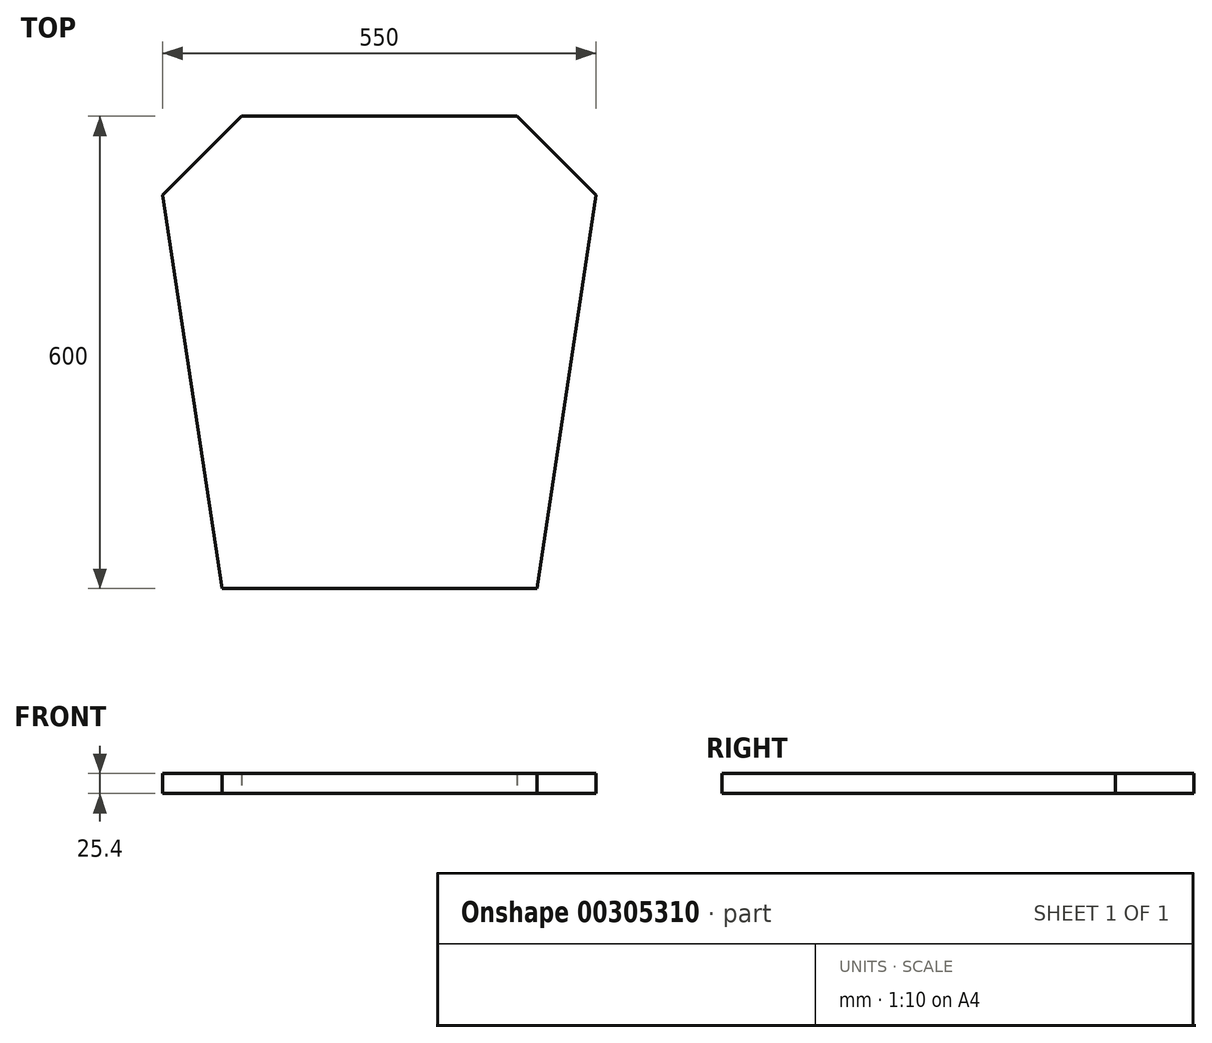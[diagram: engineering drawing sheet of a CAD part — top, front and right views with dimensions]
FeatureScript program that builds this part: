
annotation { "Feature Type Name" : "Feature", "Feature Type Description" : "" }
export const myFeature = defineFeature(function(context is Context, id is Id, definition is map)
    precondition{}
    {
        {
            var Q0;
            Q0=qCreatedBy(makeId("Top.planeOp"),FACE);
            var sketch = newSketch(context, id + "F0", { "sketchPlane" : qUnion([Q0])});
            skLineSegment(sketch, "E0", {"start": v(-175, 182.37) * mm, "end": v(175, 182.37) * mm});
            skLineSegment(sketch, "E1", {"start": v(175, 182.37) * mm, "end": v(275, 82.37) * mm});
            skLineSegment(sketch, "E2", {"start": v(275, 82.37) * mm, "end": v(200, -417.63) * mm});
            skLineSegment(sketch, "E3", {"start": v(200, -417.63) * mm, "end": v(-200, -417.63) * mm});
            skLineSegment(sketch, "E4", {"start": v(-200, -417.63) * mm, "end": v(-275, 82.37) * mm});
            skLineSegment(sketch, "E5", {"start": v(-275, 82.37) * mm, "end": v(-175, 182.37) * mm});
            skLineSegment(sketch, "E6", {"start": v(0, 182.37) * mm, "end": v(0, -417.63) * mm});
            skLineSegment(sketch, "E7", {"start": v(-275, 82.37) * mm, "end": v(-275, 182.37) * mm, "construction": true});
            skLineSegment(sketch, "E8", {"start": v(-275, 182.37) * mm, "end": v(-175, 182.37) * mm, "construction": true});
            skLineSegment(sketch, "E9", {"start": v(175, 182.37) * mm, "end": v(275, 182.37) * mm, "construction": true});
            skLineSegment(sketch, "E10", {"start": v(275, 182.37) * mm, "end": v(275, 82.37) * mm, "construction": true});
            skSolve(sketch);
        }
        {
            var Q0;
            {var subQ1=sQuery(id+"F0.wireOp",EDGE,"E4");Q0=makeQuery(id+"F0.imprint","IMPRINT",FACE,{"disambiguationData":[TD([[makeQuery(id+"F0.imprint","IMPRINT",EDGE,{"derivedFrom":subQ1}),-1.0]])]});}
            var Q1;
            {var subQ3=sQuery(id+"F0.wireOp",EDGE,"E1");Q1=makeQuery(id+"F0.imprint","IMPRINT",FACE,{"disambiguationData":[TD([[makeQuery(id+"F0.imprint","IMPRINT",EDGE,{"derivedFrom":subQ3}),-1.0]])]});}
            extrude(context, id + "F1", {"entities" : qUnion([Q0, Q1]), "depth" : 25.4 * mm});
        }
    });
